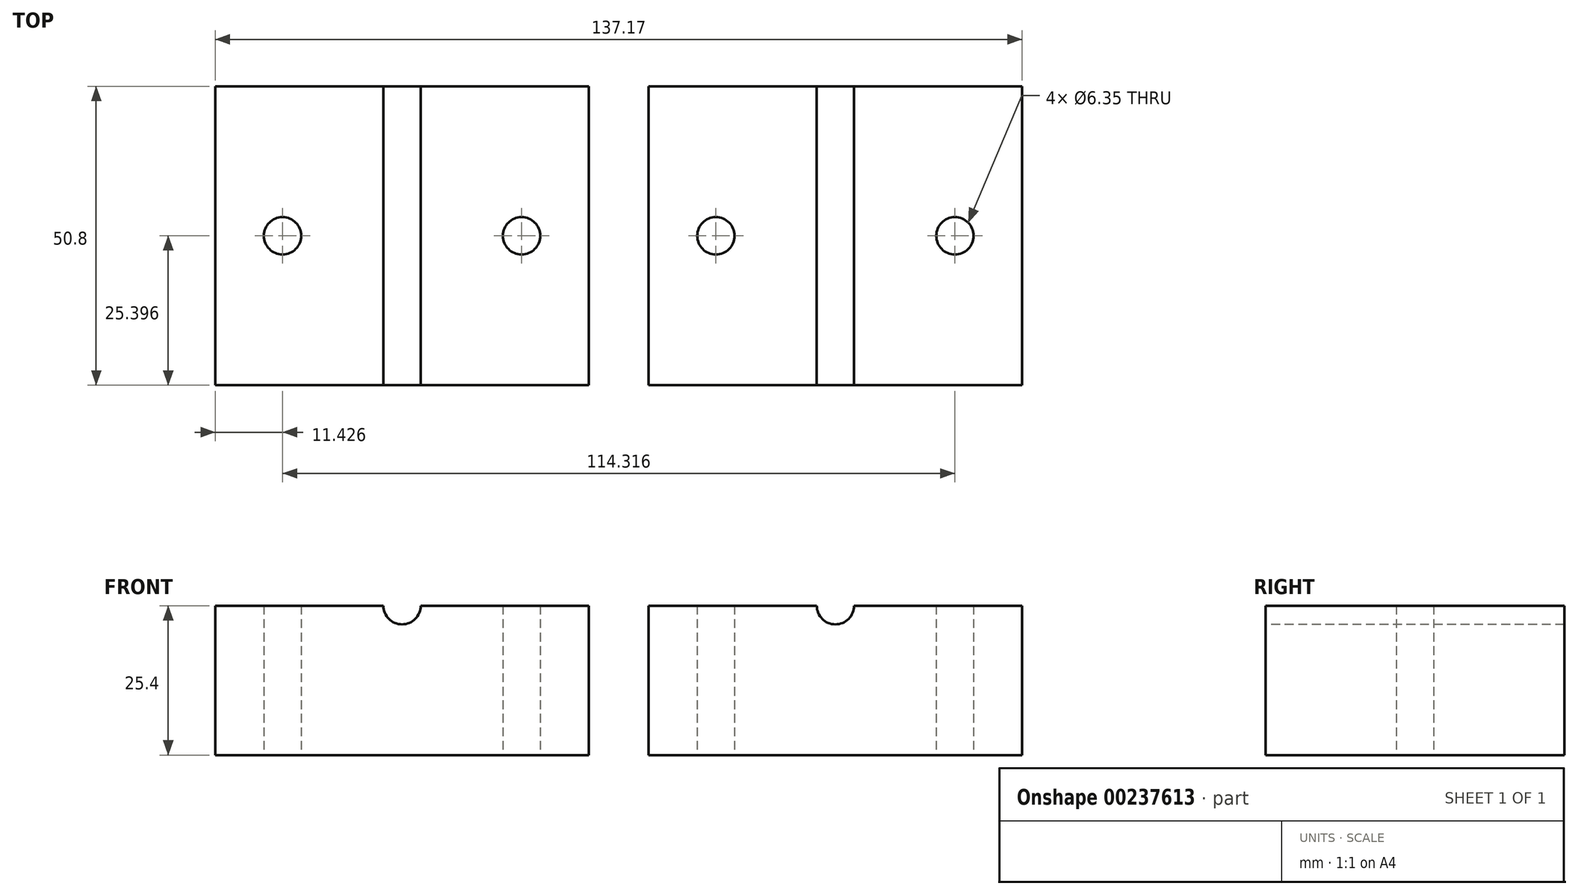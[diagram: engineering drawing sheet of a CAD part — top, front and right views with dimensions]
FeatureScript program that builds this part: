
annotation { "Feature Type Name" : "Feature", "Feature Type Description" : "" }
export const myFeature = defineFeature(function(context is Context, id is Id, definition is map)
    precondition{}
    {
        {
            var Q0;
            Q0=qCreatedBy(makeId("Top.planeOp"),FACE);
            var sketch = newSketch(context, id + "F0", { "sketchPlane" : qUnion([Q0])});
            skLineSegment(sketch, "E0.bottom", {"start": v(-59.8, 32.84) * mm, "end": v(3.7, 32.84) * mm});
            skLineSegment(sketch, "E0.top", {"start": v(-59.8, -17.96) * mm, "end": v(3.7, -17.96) * mm});
            skLineSegment(sketch, "E0.left", {"start": v(-59.8, 32.84) * mm, "end": v(-59.8, -17.96) * mm});
            skLineSegment(sketch, "E0.right", {"start": v(3.7, 32.84) * mm, "end": v(3.7, -17.96) * mm});
            skLineSegment(sketch, "E1", {"start": v(-28.05, 32.84) * mm, "end": v(-28.05, -17.96) * mm, "construction": true});
            skCircle(sketch, "E2", {"center": v(-48.37, 7.44) * mm, "radius": 3.18 * mm});
            skPoint(sketch, "E2.centerSnap0", {"position": v(-28.05, 7.44) * mm});
            skCircle(sketch, "E3", {"center": v(-7.73, 7.44) * mm, "radius": 3.18 * mm});
            skLineSegment(sketch, "E4", {"start": v(-7.73, 7.44) * mm, "end": v(3.7, 7.44) * mm, "construction": true});
            skLineSegment(sketch, "E5", {"start": v(-59.8, 7.44) * mm, "end": v(-48.37, 7.44) * mm, "construction": true});
            skLineSegment(sketch, "E6.bottom", {"start": v(13.87, 32.84) * mm, "end": v(77.37, 32.84) * mm});
            skLineSegment(sketch, "E6.top", {"start": v(13.87, -17.96) * mm, "end": v(77.37, -17.96) * mm});
            skLineSegment(sketch, "E6.left", {"start": v(13.87, 32.84) * mm, "end": v(13.87, -17.96) * mm});
            skLineSegment(sketch, "E6.right", {"start": v(77.37, 32.84) * mm, "end": v(77.37, -17.96) * mm});
            skLineSegment(sketch, "E7", {"start": v(45.62, 32.84) * mm, "end": v(45.62, -17.96) * mm, "construction": true});
            skCircle(sketch, "E8", {"center": v(25.3, 7.44) * mm, "radius": 3.18 * mm});
            skPoint(sketch, "E8.centerSnap0", {"position": v(45.62, 7.44) * mm});
            skCircle(sketch, "E9", {"center": v(65.94, 7.44) * mm, "radius": 3.18 * mm});
            skLineSegment(sketch, "E10", {"start": v(13.87, 7.44) * mm, "end": v(25.3, 7.44) * mm, "construction": true});
            skLineSegment(sketch, "E11", {"start": v(77.37, 7.44) * mm, "end": v(65.94, 7.44) * mm, "construction": true});
            skSolve(sketch);
        }
        {
            var Q0;
            Q0 = qSketchRegion(id + "F0", true);
            extrude(context, id + "F1", {"entities" : qUnion([Q0]), "depth" : 25.4 * mm});
        }
        {
            var Q0;
            Q0=makeQuery(id+"F1.opExtrude","SWEPT_FACE",FACE,{"disambiguationData":[OSD([sQuery(id+"F0.wireOp",EDGE,"E0.top")])]});
            var sketch = newSketch(context, id + "F2", { "sketchPlane" : qUnion([Q0])});
            skCircle(sketch, "E12", {"center": v(-28.05, 25.4) * mm, "radius": 3.18 * mm});
            skLineSegment(sketch, "E13.0", {"start": v(13.87, 25.4) * mm, "end": v(77.37, 25.4) * mm});
            skCircle(sketch, "E14", {"center": v(45.62, 25.4) * mm, "radius": 3.18 * mm});
            skSolve(sketch);
        }
        {
            var Q0;
            Q0 = qSketchRegion(id + "F2", true);
            extrude(context, id + "F3", {"entities" : qUnion([Q0]), "operationType" : NewBodyOperationType.REMOVE, "endBound" : BoundingType.THROUGH_ALL, "oppositeDirection" : true, "depth" : 25.4 * mm});
        }
    });
